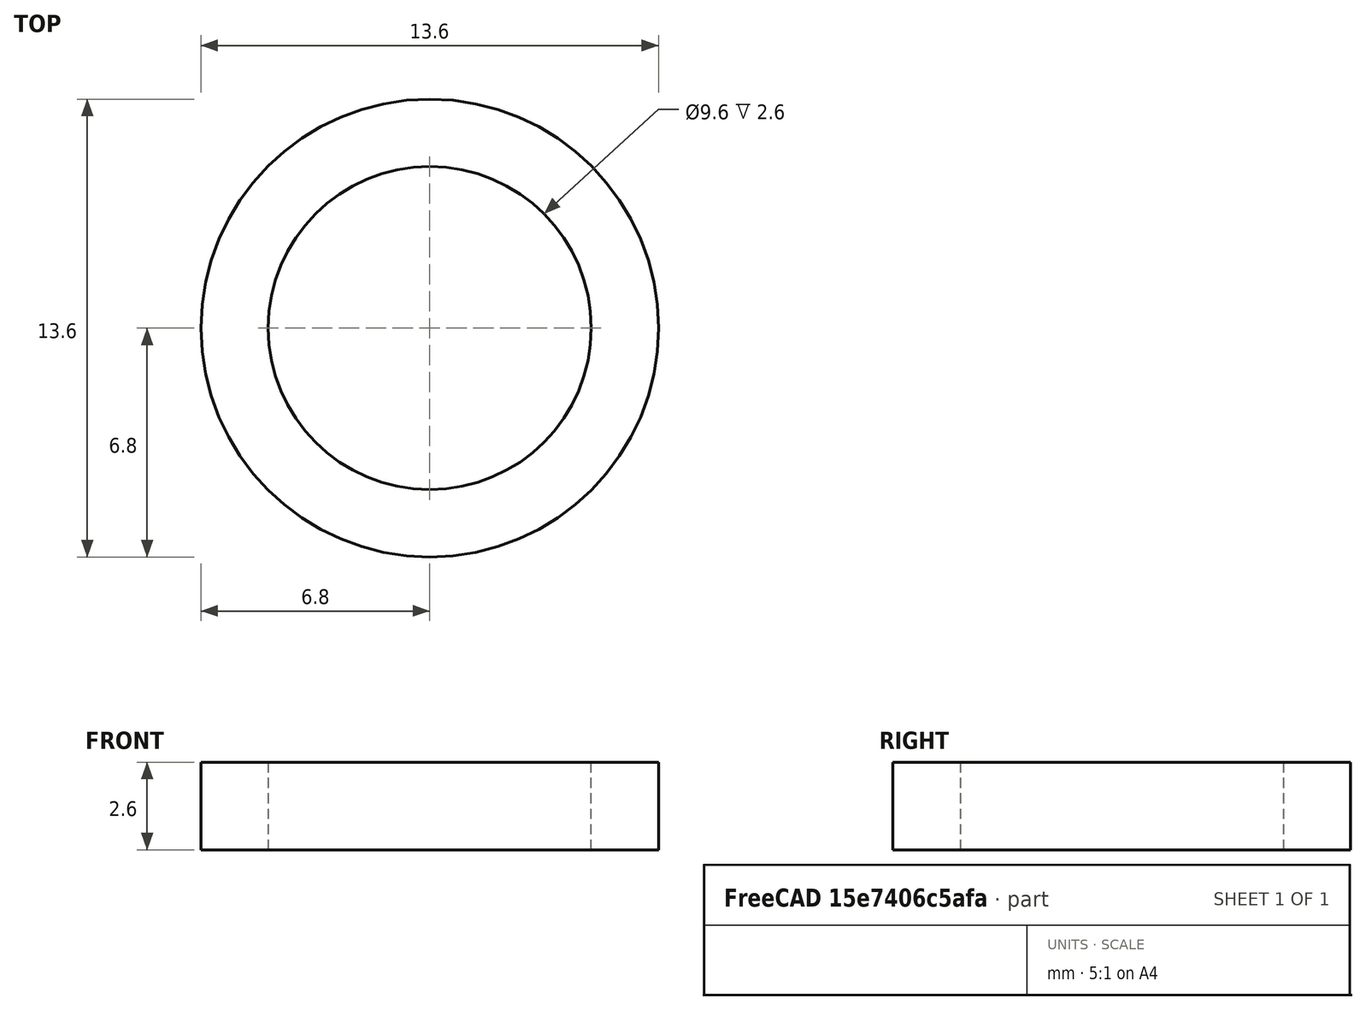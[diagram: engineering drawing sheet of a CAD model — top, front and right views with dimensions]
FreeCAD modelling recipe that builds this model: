
FCSTD DOCUMENT  (FreeCAD 0.21R33771 (Git))
Label: arruela-espacadora 
License: All rights reserved
LicenseURL: https://en.wikipedia.org/wiki/All_rights_reserved
objects: Sketcher::SketchObject×1, PartDesign::Pad×1, PartDesign::Body×1
note: 4 computed .brp shape members not serialized (recipe doc carries the construction recipe); baked Part::Feature solids carry a one-line shape summary decoded from their .brp

FEATURE [Sketcher::SketchObject] Sketch
  FullyConstrained = true
  MapMode = 5
  Support = -> [XY_Plane]
  sketch-geometry (2):
    g0: Circle CenterX=0 CenterY=0 CenterZ=0 NormalX=0 NormalY=0 NormalZ=1 AngleXU=0 Radius=4.8
    g1: Circle CenterX=0 CenterY=0 CenterZ=0 NormalX=0 NormalY=0 NormalZ=1 AngleXU=0 Radius=6.8
  constraints (4):
    c: Coincident(g0,g-1)
    c: Coincident(g1,g0)
    c: Diameter(g0) = 9.6
    c: Diameter(g1) = 13.6
FEATURE [PartDesign::Pad] Pad
  Direction = (0,0,1)
  Length = 2.6
  Length2 = 10
  Profile = -> Sketch
  ReferenceAxis = -> Sketch [N_Axis]
  Type = 0
FEATURE [PartDesign::Body] Body
  Group = -> [Sketch,Pad]
  Origin = -> Origin
  Tip = -> Pad
